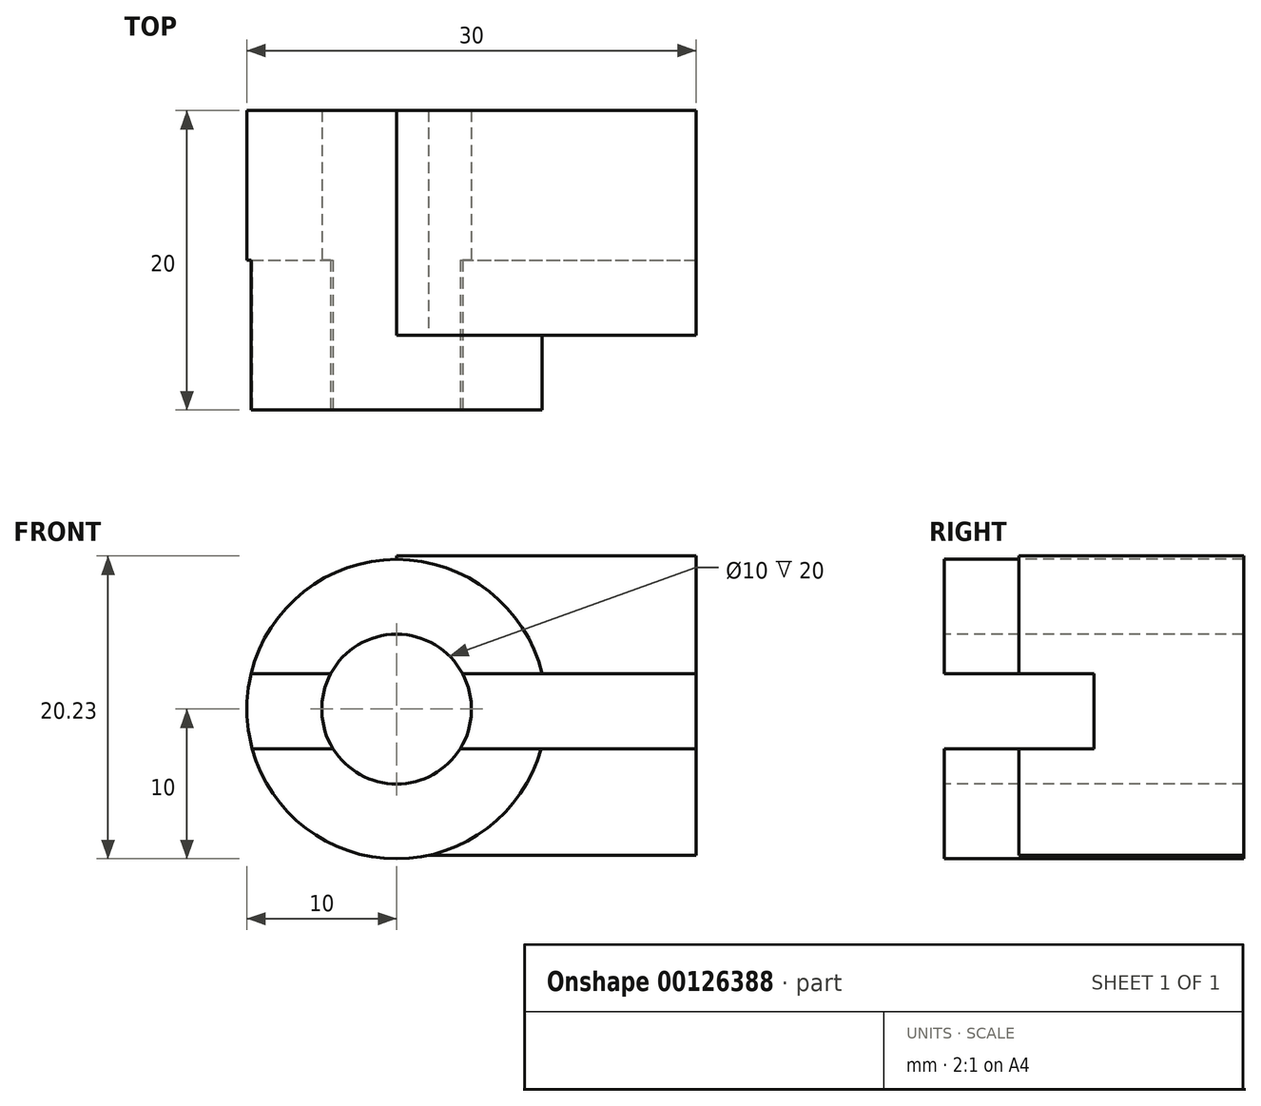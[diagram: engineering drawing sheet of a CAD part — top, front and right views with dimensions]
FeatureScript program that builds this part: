
annotation { "Feature Type Name" : "Feature", "Feature Type Description" : "" }
export const myFeature = defineFeature(function(context is Context, id is Id, definition is map)
    precondition{}
    {
        {
            var Q0;
            Q0=qCreatedBy(makeId("Front.planeOp"),FACE);
            var sketch = newSketch(context, id + "F0", { "sketchPlane" : qUnion([Q0])});
            skCircle(sketch, "E0", {"center": v(0, 0) * mm, "radius": 5 * mm});
            skCircle(sketch, "E1", {"center": v(0, 0) * mm, "radius": 10 * mm});
            skSolve(sketch);
        }
        {
            var Q0;
            Q0 = qSketchRegion(id + "F0", true);
            extrude(context, id + "F1", {"entities" : qUnion([Q0]), "oppositeDirection" : true, "depth" : 20 * mm});
        }
        {
            var Q0;
            Q0=qCreatedBy(makeId("Right.planeOp"),FACE);
            var sketch = newSketch(context, id + "F2", { "sketchPlane" : qUnion([Q0])});
            skLineSegment(sketch, "E2", {"start": v(3.95, 131.75) * mm, "end": v(18.95, 131.75) * mm});
            skLineSegment(sketch, "E3.bottom", {"start": v(20, 10.23) * mm, "end": v(5, 10.23) * mm});
            skLineSegment(sketch, "E3.top", {"start": v(20, -9.77) * mm, "end": v(5, -9.77) * mm});
            skLineSegment(sketch, "E3.left", {"start": v(20, 10.23) * mm, "end": v(20, -9.77) * mm});
            skLineSegment(sketch, "E3.right", {"start": v(5, 10.23) * mm, "end": v(5, -9.77) * mm});
            skSolve(sketch);
        }
        {
            var Q0;
            Q0 = qSketchRegion(id + "F2", true);
            extrude(context, id + "F3", {"entities" : qUnion([Q0]), "operationType" : NewBodyOperationType.ADD, "depth" : 20 * mm});
        }
        {
            var Q0;
            Q0=qCreatedBy(makeId("Front.planeOp"),FACE);
            var sketch = newSketch(context, id + "F4", { "sketchPlane" : qUnion([Q0])});
            skCircle(sketch, "E4", {"center": v(0, 0) * mm, "radius": 5 * mm});
            skSolve(sketch);
        }
        {
            var Q0;
            Q0 = qSketchRegion(id + "F4", true);
            extrude(context, id + "F5", {"entities" : qUnion([Q0]), "operationType" : NewBodyOperationType.REMOVE, "endBound" : BoundingType.THROUGH_ALL, "oppositeDirection" : true, "depth" : 25 * mm});
        }
        {
            var Q0;
            Q0=qCreatedBy(makeId("Right.planeOp"),FACE);
            var sketch = newSketch(context, id + "F6", { "sketchPlane" : qUnion([Q0])});
            skLineSegment(sketch, "E5.bottom", {"start": v(0, 2.36) * mm, "end": v(10, 2.36) * mm});
            skLineSegment(sketch, "E5.top", {"start": v(0, -2.64) * mm, "end": v(10, -2.64) * mm});
            skLineSegment(sketch, "E5.left", {"start": v(0, 2.36) * mm, "end": v(0, -2.64) * mm});
            skLineSegment(sketch, "E5.right", {"start": v(10, 2.36) * mm, "end": v(10, -2.64) * mm});
            skSolve(sketch);
        }
        {
            var Q0;
            Q0 = qSketchRegion(id + "F6", true);
            extrude(context, id + "F7", {"entities" : qUnion([Q0]), "operationType" : NewBodyOperationType.REMOVE, "endBound" : BoundingType.THROUGH_ALL, "oppositeDirection" : true, "depth" : 25 * mm, "hasSecondDirection" : true, "secondDirectionBound" : SecondDirectionBoundingType.THROUGH_ALL, "secondDirectionOppositeDirection" : false, "secondDirectionDepth" : 25 * mm});
        }
    });
